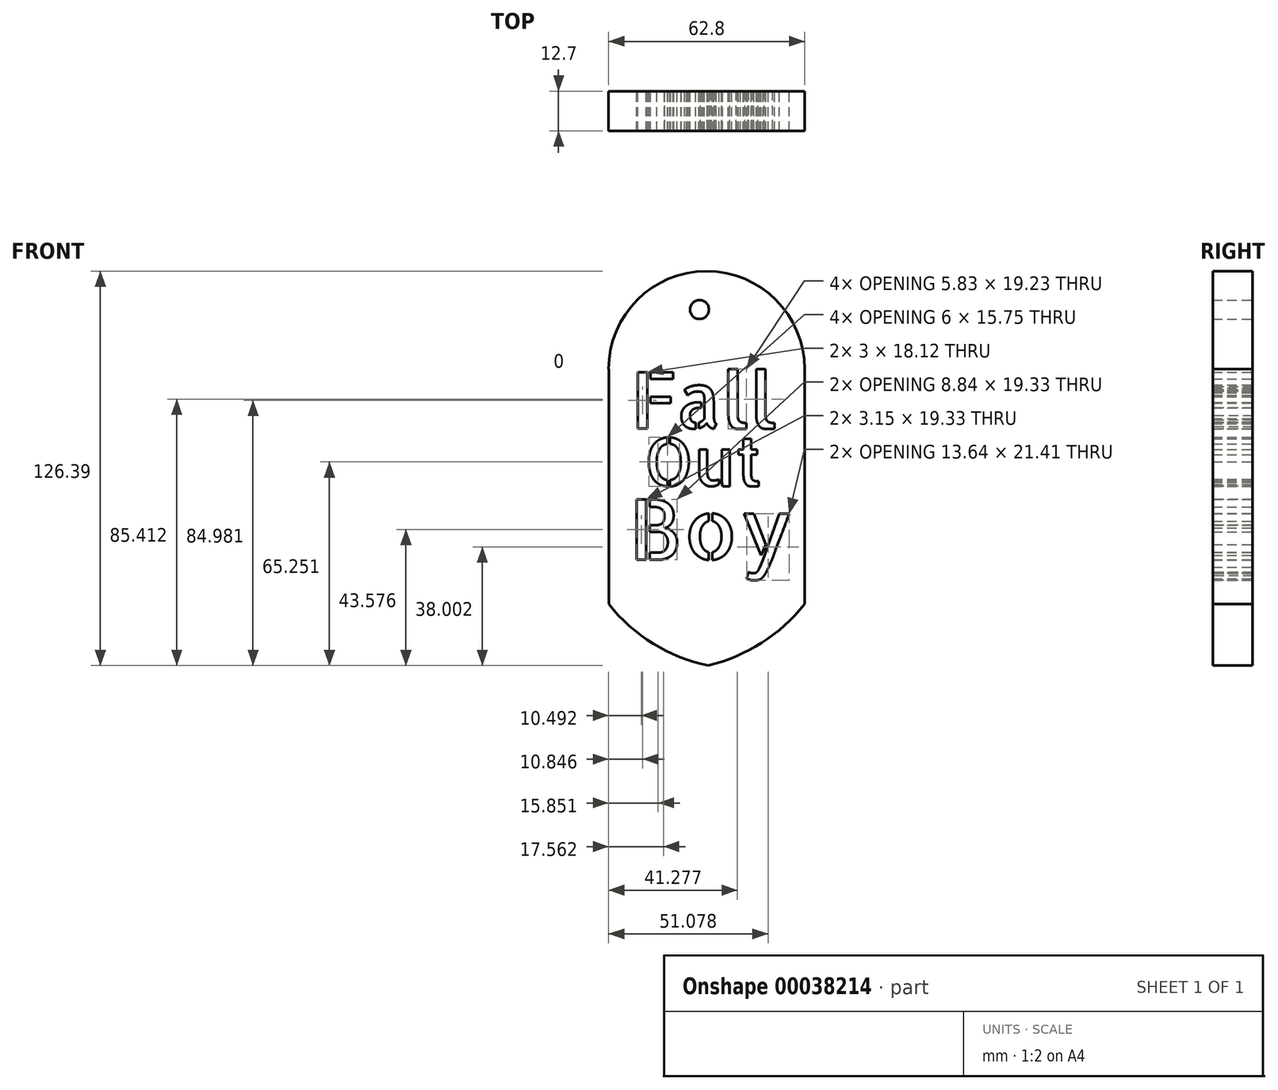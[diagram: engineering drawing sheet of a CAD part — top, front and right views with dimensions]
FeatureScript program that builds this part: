
annotation { "Feature Type Name" : "Feature", "Feature Type Description" : "" }
export const myFeature = defineFeature(function(context is Context, id is Id, definition is map)
    precondition{}
    {
        {
            var Q0;
            Q0=qCreatedBy(makeId("Front.planeOp"),FACE);
            var sketch = newSketch(context, id + "F0", { "sketchPlane" : qUnion([Q0])});
            skLineSegment(sketch, "E0.bottom", {"start": v(-29.12, 37.5) * mm, "end": v(-29.1, 37.5) * mm});
            skLineSegment(sketch, "E0.left", {"start": v(-29.1, 37.5) * mm, "end": v(-29.1, -37.8) * mm});
            skLineSegment(sketch, "E0.right", {"start": v(33.66, 37.5) * mm, "end": v(33.66, -37.8) * mm});
            skArc(sketch, "E1", {"start": v(33.68, 37.5) * mm, "mid": v(2.28, 68.91) * mm, "end": v(-29.12, 37.5) * mm});
            skArc(sketch, "E2", {"start": v(-29.1, -37.8) * mm, "mid": v(-14.86, -50.46) * mm, "end": v(2.85, -57.48) * mm});
            skArc(sketch, "E3", {"start": v(2.85, -57.48) * mm, "mid": v(19.9, -50.2) * mm, "end": v(33.66, -37.8) * mm});
            skLineSegment(sketch, "E4.trimOffspring", {"start": v(33.66, 37.5) * mm, "end": v(33.68, 37.5) * mm});
            skText(sketch, "E5", { "text": "Fall", "fontName": "AllertaStencil-Regular.ttf"});
            skText(sketch, "E6", { "text": "Out", "fontName": "AllertaStencil-Regular.ttf"});
            skText(sketch, "E7", { "text": "Boy", "fontName": "AllertaStencil-Regular.ttf"});
            skCircle(sketch, "E8", {"center": v(0, 56.62) * mm, "radius": 3.03 * mm});
            const initialGuessF0  = {"E5": [-0.02211, 0.01844, 1, 0, 0.01813], "E6": [-0.01788, 0, 1, 0, 0.01542], "E7": [-0.02272, -0.02357, 1, 0, 0.01934]};
            skSetInitialGuess(sketch, initialGuessF0);
            skSolve(sketch);
        }
        {
            var Q0;
            Q0=makeQuery(id+"F0.imprint","IMPRINT",FACE,{"disambiguationData":[TD([[makeQuery(id+"F0.imprint","IMPRINT",EDGE,{"derivedFrom":sQuery(id+"F0.wireOp",EDGE,"E0.bottom")}),1.0]])]});
            extrude(context, id + "F1", {"entities" : qUnion([Q0]), "depth" : 12.7 * mm});
        }
    });
